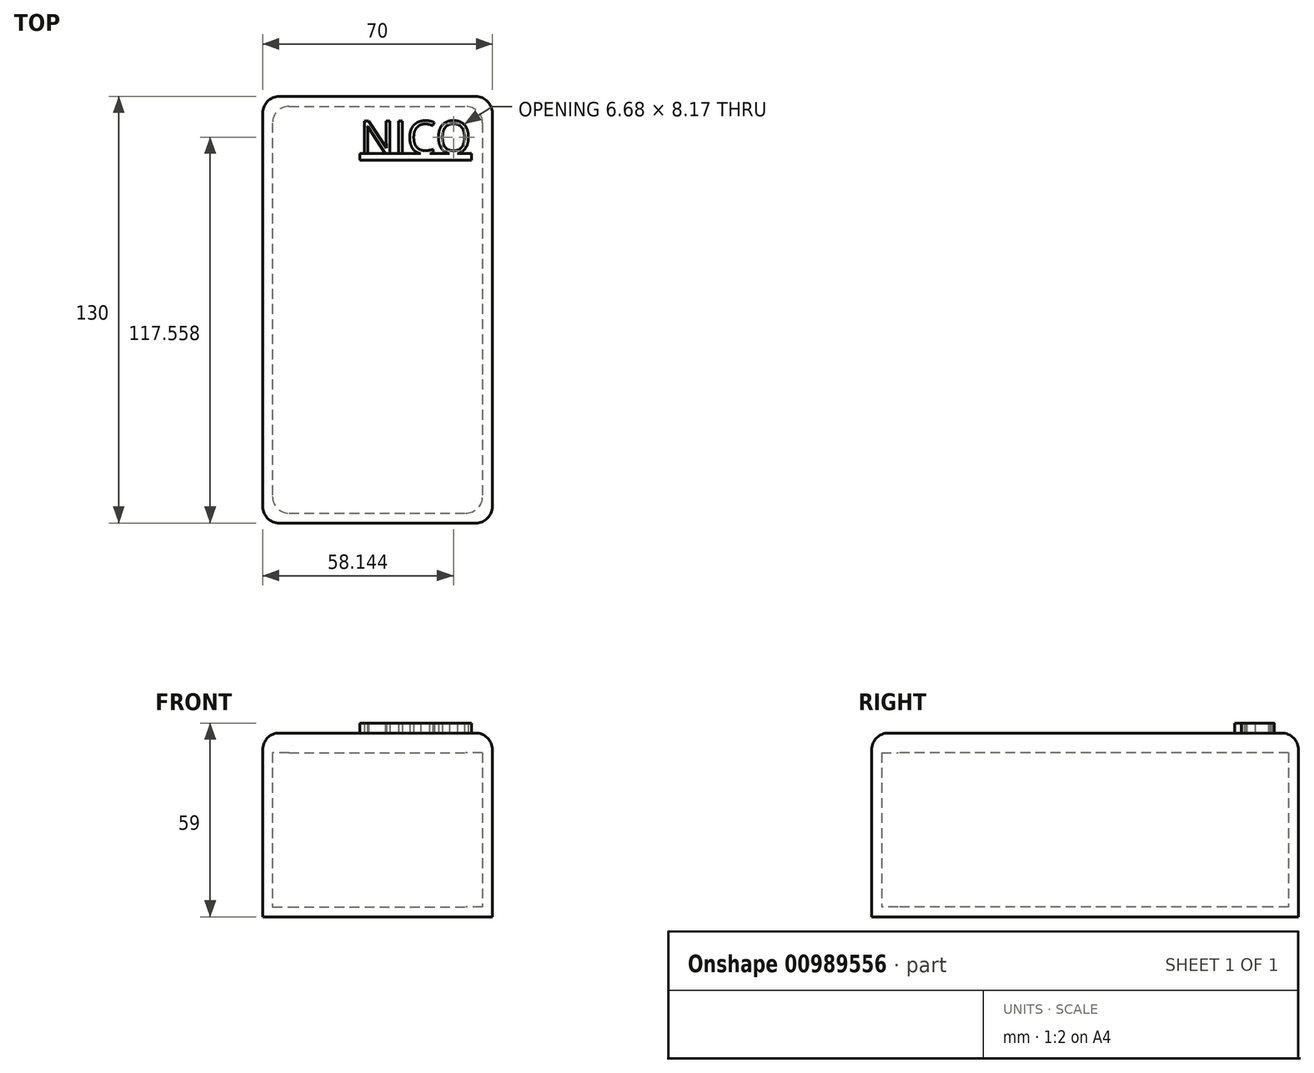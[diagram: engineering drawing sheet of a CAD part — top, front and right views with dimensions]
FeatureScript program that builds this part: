
annotation { "Feature Type Name" : "Feature", "Feature Type Description" : "" }
export const myFeature = defineFeature(function(context is Context, id is Id, definition is map)
    precondition{}
    {
        {
            var Q0;
            Q0=qCreatedBy(makeId("Top.planeOp"),FACE);
            var sketch = newSketch(context, id + "F0", { "sketchPlane" : qUnion([Q0])});
            skLineSegment(sketch, "E0.bottom", {"start": v(-35, 65) * mm, "end": v(35, 65) * mm});
            skLineSegment(sketch, "E0.top", {"start": v(-35, -65) * mm, "end": v(35, -65) * mm});
            skLineSegment(sketch, "E0.left", {"start": v(-35, 65) * mm, "end": v(-35, -65) * mm});
            skLineSegment(sketch, "E0.right", {"start": v(35, 65) * mm, "end": v(35, -65) * mm});
            skPoint(sketch, "E0.middle", {"position": v(0, 0) * mm});
            skLineSegment(sketch, "E1.bottom", {"start": v(-32, 62) * mm, "end": v(32, 62) * mm});
            skLineSegment(sketch, "E1.top", {"start": v(-32, -62) * mm, "end": v(32, -62) * mm});
            skLineSegment(sketch, "E1.left", {"start": v(-32, 62) * mm, "end": v(-32, -62) * mm});
            skLineSegment(sketch, "E1.right", {"start": v(32, 62) * mm, "end": v(32, -62) * mm});
            skSolve(sketch);
        }
        {
            var Q0;
            Q0=makeQuery(id+"F0.imprint","IMPRINT",FACE,{"disambiguationData":[TD([[makeQuery(id+"F0.imprint","IMPRINT",EDGE,{"derivedFrom":sQuery(id+"F0.wireOp",EDGE,"E0.bottom")}),-1.0]])]});
            extrude(context, id + "F1", {"entities" : qUnion([Q0]), "depth" : 50 * mm, "offsetDistance" : 25.4 * mm});
        }
        {
            var Q0;
            Q0=makeQuery(id+"F1.opExtrude","SWEPT_FACE",FACE,{"disambiguationData":[OSD([sQuery(id+"F0.wireOp",EDGE,"E0.top")])]});
            var sketch = newSketch(context, id + "F2", { "sketchPlane" : qUnion([Q0])});
            skLineSegment(sketch, "E2.left", {"start": v(-35, 0) * mm, "end": v(-35, 0) * mm});
            skLineSegment(sketch, "E2.right", {"start": v(35, 0) * mm, "end": v(35, 0) * mm});
            skPoint(sketch, "E3.oppositeSnap0", {"position": v(0, 0) * mm});
            skLineSegment(sketch, "E3.bottom", {"start": v(0, 0) * mm, "end": v(0, 0) * mm});
            skLineSegment(sketch, "E4.bottom", {"start": v(-35, 0) * mm, "end": v(35, 0) * mm});
            skLineSegment(sketch, "E4.top", {"start": v(-35, 0) * mm, "end": v(35, 0) * mm});
            skLineSegment(sketch, "E5.bottom", {"start": v(35, -3) * mm, "end": v(-35, -3) * mm});
            skLineSegment(sketch, "E5.top", {"start": v(35, 0) * mm, "end": v(-35, 0) * mm});
            skLineSegment(sketch, "E5.left", {"start": v(35, -3) * mm, "end": v(35, 0) * mm});
            skLineSegment(sketch, "E5.right", {"start": v(-35, -3) * mm, "end": v(-35, 0) * mm});
            skSolve(sketch);
        }
        {
            var Q0;
            Q0=makeQuery(id+"F2.imprint","IMPRINT",FACE,{"disambiguationData":[TD([[makeQuery(id+"F2.imprint","IMPRINT",EDGE,{"derivedFrom":sQuery(id+"F2.wireOp",EDGE,"E5.bottom")}),-1.0]])]});
            var Q1;
            Q1=makeQuery(id+"F1.opExtrude","SWEPT_FACE",FACE,{"disambiguationData":[OSD([sQuery(id+"F0.wireOp",EDGE,"E0.bottom")])]});
            extrude(context, id + "F3", {"entities" : qUnion([Q0]), "operationType" : NewBodyOperationType.ADD, "endBound" : BoundingType.UP_TO_SURFACE, "oppositeDirection" : true, "depth" : 25.4 * mm, "endBoundEntityFace" : qUnion([Q1]), "offsetDistance" : 25.4 * mm});
        }
        {
            var Q0;
            Q0=makeQuery(id+"F3.boolean.opBoolean","MERGE",EDGE,{"derivedFrom":[makeQuery(id+"F1.opExtrude","SWEPT_EDGE",EDGE,{"disambiguationData":[OSD([sQuery(id+"F0.wireOp",EDGE,"E0.bottom"),sQuery(id+"F0.wireOp",EDGE,"E0.right")])]}),makeQuery(id+"F3.opExtrude","CAP_EDGE",EDGE,{"disambiguationData":[OSD([sQuery(id+"F2.wireOp",EDGE,"E5.left")])],"isStart":false})]});
            var Q1;
            Q1=makeQuery(id+"F3.boolean.opBoolean","MERGE",EDGE,{"derivedFrom":[makeQuery(id+"F1.opExtrude","SWEPT_EDGE",EDGE,{"disambiguationData":[OSD([sQuery(id+"F0.wireOp",EDGE,"E0.bottom"),sQuery(id+"F0.wireOp",EDGE,"E0.left")])]}),makeQuery(id+"F3.opExtrude","CAP_EDGE",EDGE,{"disambiguationData":[OSD([sQuery(id+"F2.wireOp",EDGE,"E5.right")])],"isStart":false})]});
            var Q2;
            Q2=makeQuery(id+"F3.boolean.opBoolean","MERGE",EDGE,{"derivedFrom":[makeQuery(id+"F1.opExtrude","SWEPT_EDGE",EDGE,{"disambiguationData":[OSD([sQuery(id+"F0.wireOp",EDGE,"E0.top"),sQuery(id+"F0.wireOp",EDGE,"E0.left")])]}),makeQuery(id+"F3.opExtrude","CAP_EDGE",EDGE,{"disambiguationData":[OSD([sQuery(id+"F2.wireOp",EDGE,"E5.right")])],"isStart":true})]});
            var Q3;
            Q3=makeQuery(id+"F3.boolean.opBoolean","MERGE",EDGE,{"derivedFrom":[makeQuery(id+"F1.opExtrude","SWEPT_EDGE",EDGE,{"disambiguationData":[OSD([sQuery(id+"F0.wireOp",EDGE,"E0.top"),sQuery(id+"F0.wireOp",EDGE,"E0.right")])]}),makeQuery(id+"F3.opExtrude","CAP_EDGE",EDGE,{"disambiguationData":[OSD([sQuery(id+"F2.wireOp",EDGE,"E5.left")])],"isStart":true})]});
            fillet(context, id + "F4", {"entities" : qUnion([Q0, Q1, Q2, Q3]), "radius" : 5.08 * mm, "tangentPropagation" : true, "allowEdgeOverflow" : false});
        }
        {
            var Q0;
            Q0=makeQuery(id+"F1.opExtrude","SWEPT_EDGE",EDGE,{"disambiguationData":[OSD([sQuery(id+"F0.wireOp",EDGE,"E1.top"),sQuery(id+"F0.wireOp",EDGE,"E1.left")])]});
            var Q1;
            Q1=makeQuery(id+"F1.opExtrude","SWEPT_EDGE",EDGE,{"disambiguationData":[OSD([sQuery(id+"F0.wireOp",EDGE,"E1.bottom"),sQuery(id+"F0.wireOp",EDGE,"E1.left")])]});
            var Q2;
            Q2=makeQuery(id+"F1.opExtrude","SWEPT_EDGE",EDGE,{"disambiguationData":[OSD([sQuery(id+"F0.wireOp",EDGE,"E1.bottom"),sQuery(id+"F0.wireOp",EDGE,"E1.right")])]});
            var Q3;
            Q3=makeQuery(id+"F1.opExtrude","SWEPT_EDGE",EDGE,{"disambiguationData":[OSD([sQuery(id+"F0.wireOp",EDGE,"E1.top"),sQuery(id+"F0.wireOp",EDGE,"E1.right")])]});
            fillet(context, id + "F5", {"entities" : qUnion([Q0, Q1, Q2, Q3]), "radius" : 5.08 * mm, "tangentPropagation" : true, "allowEdgeOverflow" : false});
        }
        {
            var Q0;
            Q0=makeQuery(id+"F1.opExtrude","CAP_FACE",FACE,{"disambiguationData":[OSD([sQuery(id+"F0.wireOp",EDGE,"E0.bottom"),sQuery(id+"F0.wireOp",EDGE,"E0.top"),sQuery(id+"F0.wireOp",EDGE,"E0.left"),sQuery(id+"F0.wireOp",EDGE,"E0.right"),sQuery(id+"F0.wireOp",EDGE,"E1.bottom"),sQuery(id+"F0.wireOp",EDGE,"E1.top"),sQuery(id+"F0.wireOp",EDGE,"E1.left"),sQuery(id+"F0.wireOp",EDGE,"E1.right")])],"isStart":false});
            var sketch = newSketch(context, id + "F6", { "sketchPlane" : qUnion([Q0])});
            skPoint(sketch, "E6.middle", {"position": v(0, 0) * mm});
            skLineSegment(sketch, "E7.bottom", {"start": v(-32, 62) * mm, "end": v(32, 62) * mm});
            skLineSegment(sketch, "E7.top", {"start": v(-32, -62) * mm, "end": v(32, -62) * mm});
            skLineSegment(sketch, "E7.left", {"start": v(-32, 62) * mm, "end": v(-32, -62) * mm});
            skLineSegment(sketch, "E7.right", {"start": v(32, 62) * mm, "end": v(32, -62) * mm});
            skSolve(sketch);
        }
        {
            var Q0;
            {var subQ1=sQuery(id+"F0.wireOp",EDGE,"E1.right");var subQ2=sQuery(id+"F0.wireOp",EDGE,"E1.left");var subQ3=sQuery(id+"F0.wireOp",EDGE,"E1.top");var subQ4=sQuery(id+"F0.wireOp",EDGE,"E1.bottom");var subQ5=makeQuery(id+"F1.opExtrude","CAP_FACE",FACE,{"disambiguationData":[OSD([sQuery(id+"F0.wireOp",EDGE,"E0.bottom"),sQuery(id+"F0.wireOp",EDGE,"E0.top"),sQuery(id+"F0.wireOp",EDGE,"E0.left"),sQuery(id+"F0.wireOp",EDGE,"E0.right"),subQ4,subQ3,subQ2,subQ1])],"isStart":false});var subQ9=makeQuery(id+"F5.opFillet","BLEND_EDGE",EDGE,{"blendedFrom":[makeQuery(id+"F1.opExtrude","SWEPT_EDGE",EDGE,{"disambiguationData":[OSD([subQ4,subQ2])]}),subQ5],"blendedInto":[subQ5]});Q0=makeQuery(id+"F6.imprint","IMPRINT",FACE,{"disambiguationData":[TD([[makeQuery(id+"F6.imprint","IMPRINT",EDGE,{"derivedFrom":subQ9}),-1.0]])]});}
            extrude(context, id + "F7", {"entities" : qUnion([Q0]), "oppositeDirection" : true, "depth" : 3 * mm, "offsetDistance" : 25.4 * mm});
        }
        {
            var Q0;
            Q0=makeQuery(id+"F7.opExtrude","CAP_FACE",FACE,{"disambiguationData":[OSD([sQuery(id+"F0.wireOp",EDGE,"E0.bottom"),sQuery(id+"F0.wireOp",EDGE,"E0.top"),sQuery(id+"F0.wireOp",EDGE,"E0.left"),sQuery(id+"F0.wireOp",EDGE,"E0.right"),sQuery(id+"F0.wireOp",EDGE,"E1.bottom"),sQuery(id+"F0.wireOp",EDGE,"E1.top"),sQuery(id+"F0.wireOp",EDGE,"E1.left"),sQuery(id+"F0.wireOp",EDGE,"E1.right"),sQuery(id+"F6.wireOp",EDGE,"E7.bottom"),sQuery(id+"F6.wireOp",EDGE,"E7.top"),sQuery(id+"F6.wireOp",EDGE,"E7.left"),sQuery(id+"F6.wireOp",EDGE,"E7.right")])],"isStart":true});
            var sketch = newSketch(context, id + "F8", { "sketchPlane" : qUnion([Q0])});
            skLineSegment(sketch, "E8.bottom", {"start": v(-35, 65) * mm, "end": v(35, 65) * mm});
            skLineSegment(sketch, "E8.top", {"start": v(-35, -65) * mm, "end": v(35, -65) * mm});
            skLineSegment(sketch, "E8.left", {"start": v(-35, 65) * mm, "end": v(-35, -65) * mm});
            skLineSegment(sketch, "E8.right", {"start": v(35, 65) * mm, "end": v(35, -65) * mm});
            skPoint(sketch, "E8.middle", {"position": v(0, 0) * mm});
            skSolve(sketch);
        }
        {
            var Q0;
            Q0 = qSketchRegion(id + "F8", true);
            extrude(context, id + "F9", {"entities" : qUnion([Q0]), "operationType" : NewBodyOperationType.ADD, "depth" : 3 * mm, "offsetDistance" : 25.4 * mm});
        }
        {
            var Q0;
            Q0=makeQuery(id+"F9.opExtrude","SWEPT_EDGE",EDGE,{"disambiguationData":[OSD([sQuery(id+"F8.wireOp",EDGE,"E8.bottom"),sQuery(id+"F8.wireOp",EDGE,"E8.left")])]});
            var Q1;
            Q1=makeQuery(id+"F9.opExtrude","SWEPT_EDGE",EDGE,{"disambiguationData":[OSD([sQuery(id+"F8.wireOp",EDGE,"E8.top"),sQuery(id+"F8.wireOp",EDGE,"E8.left")])]});
            var Q2;
            Q2=makeQuery(id+"F9.opExtrude","SWEPT_EDGE",EDGE,{"disambiguationData":[OSD([sQuery(id+"F8.wireOp",EDGE,"E8.top"),sQuery(id+"F8.wireOp",EDGE,"E8.right")])]});
            var Q3;
            Q3=makeQuery(id+"F9.opExtrude","SWEPT_EDGE",EDGE,{"disambiguationData":[OSD([sQuery(id+"F8.wireOp",EDGE,"E8.bottom"),sQuery(id+"F8.wireOp",EDGE,"E8.right")])]});
            fillet(context, id + "F10", {"entities" : qUnion([Q0, Q1, Q2, Q3]), "radius" : 5.08 * mm, "tangentPropagation" : true, "allowEdgeOverflow" : false});
        }
        {
            var Q0;
            Q0=makeQuery(id+"F9.opExtrude","CAP_FACE",FACE,{"disambiguationData":[OSD([sQuery(id+"F8.wireOp",EDGE,"E8.bottom"),sQuery(id+"F8.wireOp",EDGE,"E8.top"),sQuery(id+"F8.wireOp",EDGE,"E8.left"),sQuery(id+"F8.wireOp",EDGE,"E8.right")])],"isStart":false});
            var sketch = newSketch(context, id + "F11", { "sketchPlane" : qUnion([Q0])});
            skText(sketch, "E9", { "text": "NICO", "fontName": "OpenSans-Regular.ttf"});
            skLineSegment(sketch, "E10.bottom", {"start": v(-5.37, 47.6) * mm, "end": v(28.6, 47.6) * mm});
            skLineSegment(sketch, "E10.top", {"start": v(-5.37, 47.6) * mm, "end": v(28.6, 47.6) * mm});
            skLineSegment(sketch, "E10.left", {"start": v(-5.37, 47.6) * mm, "end": v(-5.37, 47.6) * mm});
            skLineSegment(sketch, "E10.right", {"start": v(28.6, 47.6) * mm, "end": v(28.6, 47.6) * mm});
            skLineSegment(sketch, "E11.bottom", {"start": v(28.6, 45.6) * mm, "end": v(-5.37, 45.6) * mm});
            skLineSegment(sketch, "E11.top", {"start": v(28.6, 47.6) * mm, "end": v(-5.37, 47.6) * mm});
            skLineSegment(sketch, "E11.left", {"start": v(28.6, 45.6) * mm, "end": v(28.6, 47.6) * mm});
            skLineSegment(sketch, "E11.right", {"start": v(-5.37, 45.6) * mm, "end": v(-5.37, 47.6) * mm});
            const initialGuessF11  = {"E9": [-0.00537, 0.0476, 1, 0, 0.01]};
            skSetInitialGuess(sketch, initialGuessF11);
            skSolve(sketch);
        }
        {
            var Q0;
            Q0 = qSketchRegion(id + "F11", true);
            var Q1;
            Q1 = qConstructionFilter(qBodyType(qCreatedBy(id + "F11" ,EDGE), BodyType.WIRE), ConstructionObject.NO);
            extrude(context, id + "F12", {"entities" : qUnion([Q0]), "surfaceEntities" : qUnion([Q1]), "depth" : 3 * mm, "offsetDistance" : 25.4 * mm});
        }
        {
            var Q0;
            Q0=makeQuery(id+"F9.opExtrude","CAP_EDGE",EDGE,{"disambiguationData":[OSD([sQuery(id+"F8.wireOp",EDGE,"E8.top")])],"isStart":false});
            fillet(context, id + "F13", {"entities" : qUnion([Q0]), "radius" : 5.08 * mm, "tangentPropagation" : true, "allowEdgeOverflow" : false});
        }
    });
